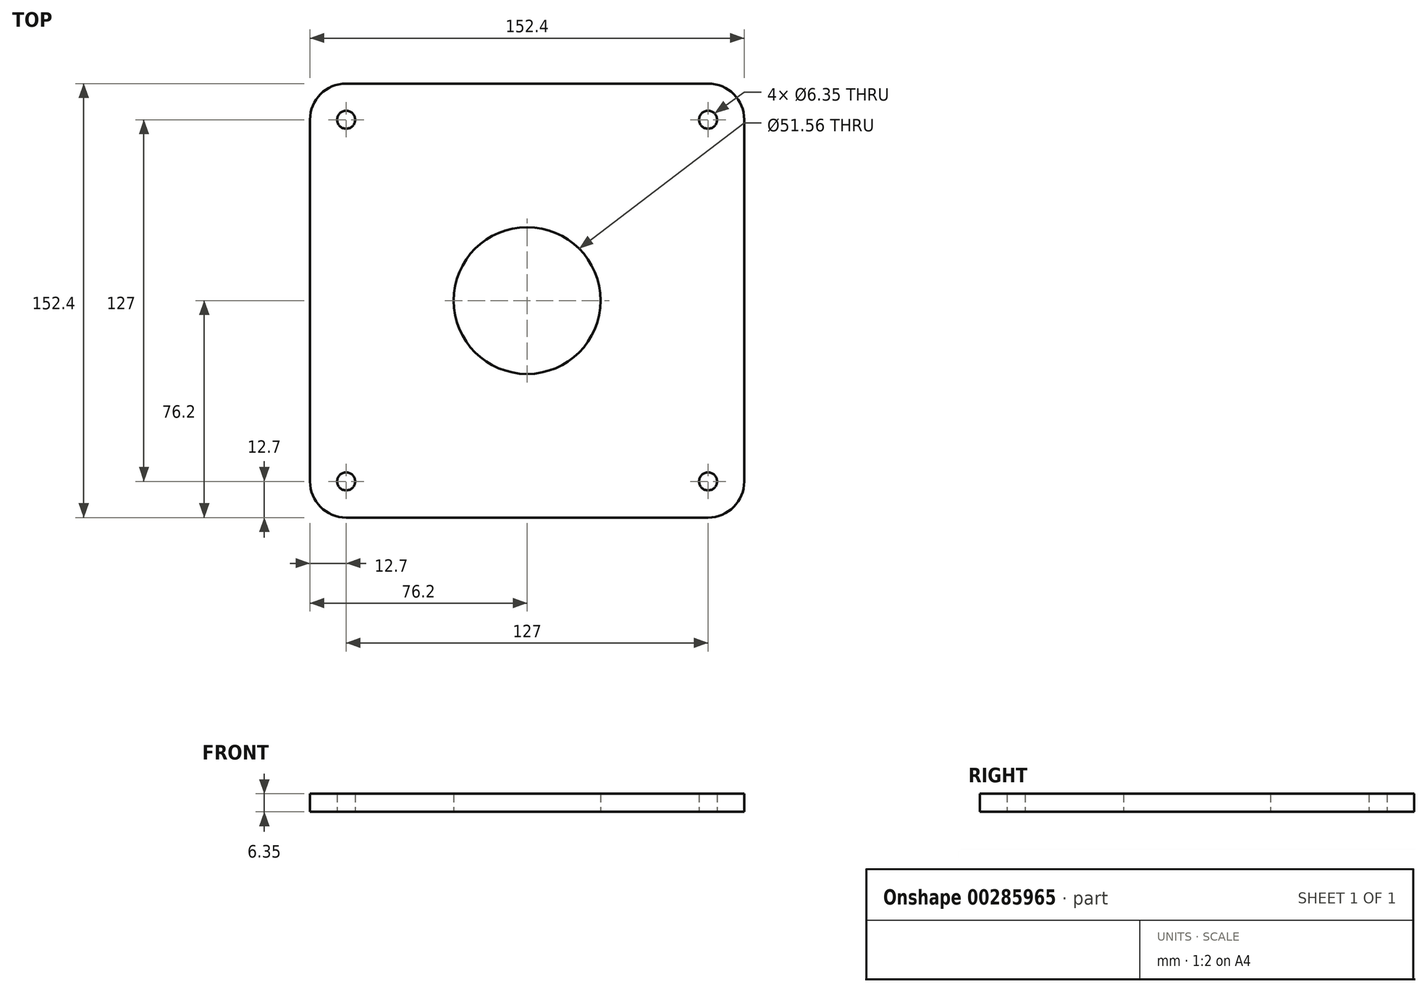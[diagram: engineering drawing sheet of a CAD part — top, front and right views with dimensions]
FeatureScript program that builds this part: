
annotation { "Feature Type Name" : "Feature", "Feature Type Description" : "" }
export const myFeature = defineFeature(function(context is Context, id is Id, definition is map)
    precondition{}
    {
        {
            var Q0;
            Q0=qCreatedBy(makeId("Top.planeOp"),FACE);
            var sketch = newSketch(context, id + "F0", { "sketchPlane" : qUnion([Q0])});
            skLineSegment(sketch, "E0.bottom", {"start": v(12.7, 0) * mm, "end": v(139.7, 0) * mm});
            skLineSegment(sketch, "E0.top", {"start": v(12.7, -152.4) * mm, "end": v(139.7, -152.4) * mm});
            skLineSegment(sketch, "E0.left", {"start": v(0, -12.7) * mm, "end": v(0, -139.7) * mm});
            skLineSegment(sketch, "E0.right", {"start": v(152.4, -12.7) * mm, "end": v(152.4, -139.7) * mm});
            skPoint(sketch, "E1.visualSharp", {"position": v(0, 0) * mm});
            skArc(sketch, "E1.filletArc", {"start": v(12.7, 0) * mm, "mid": v(3.72, -3.72) * mm, "end": v(0, -12.7) * mm});
            skPoint(sketch, "E2.visualSharp", {"position": v(152.4, 0) * mm});
            skArc(sketch, "E2.filletArc", {"start": v(152.4, -12.7) * mm, "mid": v(148.68, -3.72) * mm, "end": v(139.7, 0) * mm});
            skPoint(sketch, "E3.visualSharp", {"position": v(152.4, -152.4) * mm});
            skArc(sketch, "E3.filletArc", {"start": v(139.7, -152.4) * mm, "mid": v(148.68, -148.68) * mm, "end": v(152.4, -139.7) * mm});
            skPoint(sketch, "E4.visualSharp", {"position": v(0, -152.4) * mm});
            skArc(sketch, "E4.filletArc", {"start": v(0, -139.7) * mm, "mid": v(3.72, -148.68) * mm, "end": v(12.7, -152.4) * mm});
            skCircle(sketch, "E5", {"center": v(12.7, -12.7) * mm, "radius": 3.18 * mm});
            skCircle(sketch, "E6", {"center": v(139.7, -12.7) * mm, "radius": 3.18 * mm});
            skCircle(sketch, "E7", {"center": v(139.7, -139.7) * mm, "radius": 3.18 * mm});
            skCircle(sketch, "E8", {"center": v(12.7, -139.7) * mm, "radius": 3.18 * mm});
            skCircle(sketch, "E9", {"center": v(76.2, -76.2) * mm, "radius": 25.78 * mm});
            skSolve(sketch);
        }
        {
            var Q0;
            Q0 = qSketchRegion(id + "F0", true);
            extrude(context, id + "F1", {"entities" : qUnion([Q0]), "depth" : 6.35 * mm});
        }
    });
